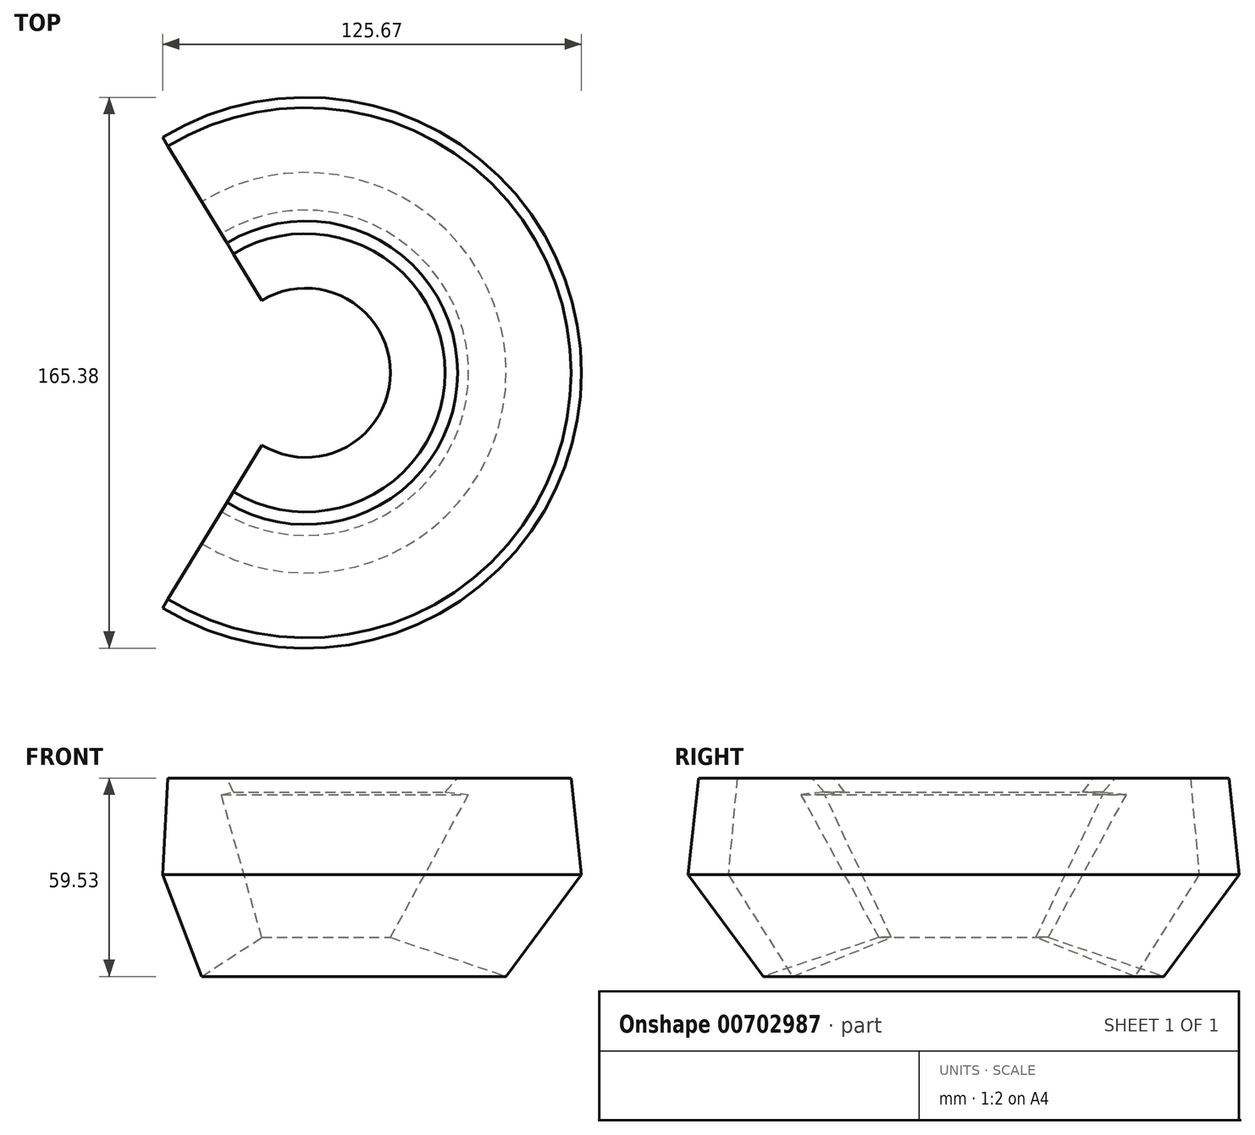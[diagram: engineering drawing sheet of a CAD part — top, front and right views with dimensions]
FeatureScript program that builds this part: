
annotation { "Feature Type Name" : "Feature", "Feature Type Description" : "" }
export const myFeature = defineFeature(function(context is Context, id is Id, definition is map)
    precondition{}
    {
        {
            var Q0;
            Q0=qCreatedBy(makeId("Front.planeOp"),FACE);
            var sketch = newSketch(context, id + "F0", { "sketchPlane" : qUnion([Q0])});
            skLineSegment(sketch, "E0", {"start": v(0, 30.47) * mm, "end": v(36.12, 30.47) * mm});
            skLineSegment(sketch, "E1", {"start": v(36.12, 30.47) * mm, "end": v(39.23, 1.45) * mm});
            skLineSegment(sketch, "E2", {"start": v(39.23, 1.45) * mm, "end": v(16.65, -29.06) * mm});
            skLineSegment(sketch, "E3", {"start": v(16.65, -29.06) * mm, "end": v(-18.06, -17.35) * mm});
            skLineSegment(sketch, "E4", {"start": v(-18.06, -17.35) * mm, "end": v(5.36, 25.54) * mm});
            skLineSegment(sketch, "E5", {"start": v(5.36, 25.54) * mm, "end": v(-1.7, 26.32) * mm});
            skLineSegment(sketch, "E6", {"start": v(-1.7, 26.32) * mm, "end": v(7.06, 35.9) * mm});
            skSolve(sketch);
        }
        {
            var Q0;
            Q0=qCreatedBy(makeId("Front.planeOp"),FACE);
            var sketch = newSketch(context, id + "F1", { "sketchPlane" : qUnion([Q0])});
            skLineSegment(sketch, "E7", {"start": v(-43.46, 80.3) * mm, "end": v(-43.46, -70.27) * mm});
            skSolve(sketch);
        }
        {
            var Q0;
            {var subQ0=sQuery(id+"F0.wireOp",EDGE,"E1");Q0=makeQuery(id+"F0.imprint","IMPRINT",FACE,{"disambiguationData":[TD([[makeQuery(id+"F0.imprint","IMPRINT",EDGE,{"derivedFrom":subQ0}),-1.0]])]});}
            var Q1;
            Q1=sQuery(id+"F1.wireOp",EDGE,"E7");
            revolve(context, id + "F2", {"surfaceOperationType" : NewSurfaceOperationType.NEW, "entities" : qUnion([Q0]), "axis" : qUnion([Q1]), "revolveType" : RevolveType.SYMMETRIC, "angle" : 242.63 * degree});
        }
    });
